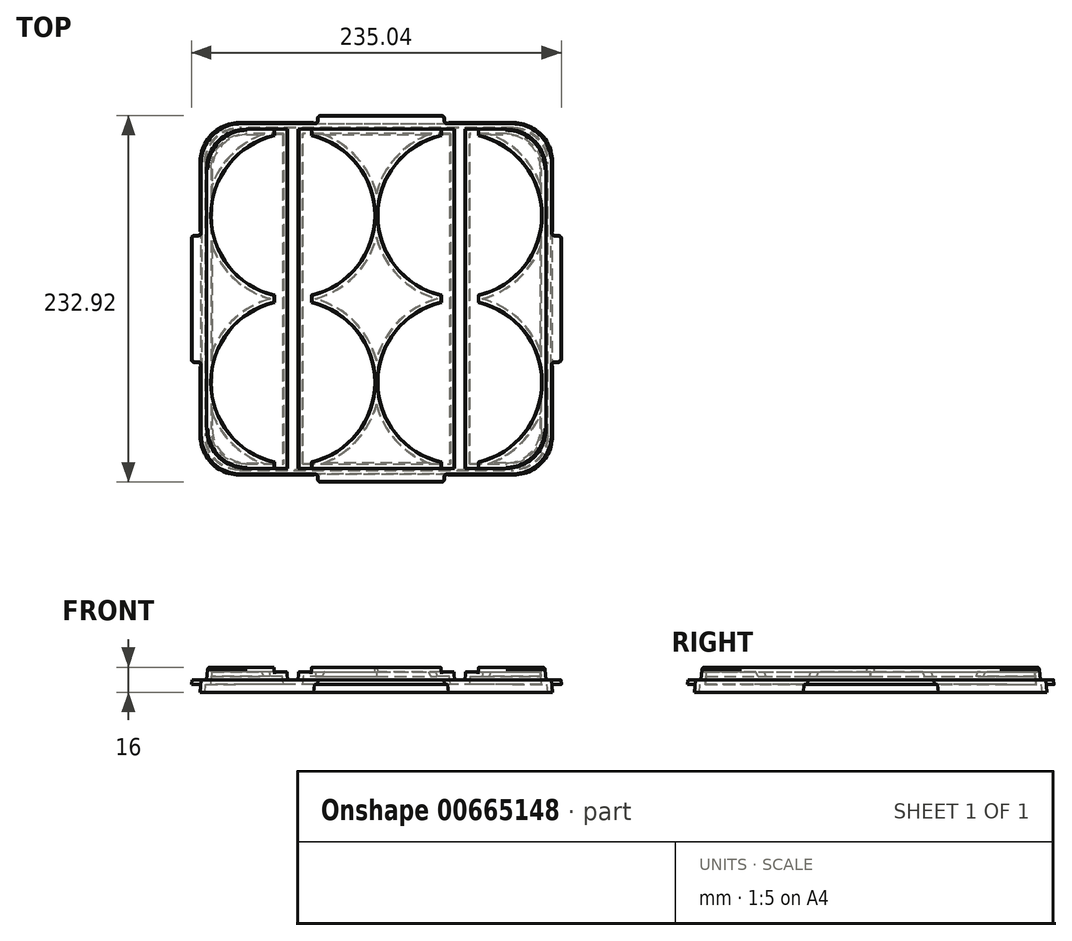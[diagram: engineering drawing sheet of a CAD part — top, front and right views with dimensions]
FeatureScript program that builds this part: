
annotation { "Feature Type Name" : "Feature", "Feature Type Description" : "" }
export const myFeature = defineFeature(function(context is Context, id is Id, definition is map)
    precondition{}
    {
        {
            var Q0;
            Q0=qCreatedBy(makeId("Top.planeOp"),FACE);
            var sketch = newSketch(context, id + "F0", { "sketchPlane" : qUnion([Q0])});
            skLineSegment(sketch, "E0", {"start": v(-53, 63.68) * mm, "end": v(-53, -68.5) * mm, "construction": true});
            skLineSegment(sketch, "E1", {"start": v(-108.87, 53) * mm, "end": v(91.95, 53) * mm, "construction": true});
            skLineSegment(sketch, "E2.MirrorCS", {"start": v(53, 63.68) * mm, "end": v(53, -68.5) * mm, "construction": true});
            skLineSegment(sketch, "E3.MirrorCS", {"start": v(-108.87, -53) * mm, "end": v(91.95, -53) * mm, "construction": true});
            skLineSegment(sketch, "E4", {"start": v(-107, 152.73) * mm, "end": v(-107, -156.18) * mm, "construction": true});
            skLineSegment(sketch, "E5", {"start": v(-201.2, -107) * mm, "end": v(310.8, -107) * mm, "construction": true});
            skLineSegment(sketch, "E6.MirrorCS", {"start": v(107, 152.73) * mm, "end": v(107, -156.18) * mm, "construction": true});
            skLineSegment(sketch, "E7.MirrorCS", {"start": v(-201.2, 107) * mm, "end": v(310.8, 107) * mm, "construction": true});
            skLineSegment(sketch, "E8.bottom", {"start": v(-107, 107) * mm, "end": v(107, 107) * mm});
            skLineSegment(sketch, "E8.top", {"start": v(-107, -107) * mm, "end": v(107, -107) * mm});
            skLineSegment(sketch, "E8.left", {"start": v(-107, 107) * mm, "end": v(-107, -107) * mm});
            skLineSegment(sketch, "E8.right", {"start": v(107, 107) * mm, "end": v(107, -107) * mm});
            skSolve(sketch);
        }
        {
            var Q0;
            Q0=makeQuery(id+"F0.imprint","IMPRINT",FACE,{"disambiguationData":[TD([[makeQuery(id+"F0.imprint","IMPRINT",EDGE,{"derivedFrom":sQuery(id+"F0.wireOp",EDGE,"E8.bottom")}),-1.0]])]});
            extrude(context, id + "F1", {"entities" : qUnion([Q0]), "oppositeDirection" : true, "depth" : 8 * mm, "offsetDistance" : 25 * mm, "hasDraft" : true, "draftAngle" : 5 * degree});
        }
        {
            var Q0;
            Q0=makeQuery(id+"F1.opExtrude","CAP_FACE",FACE,{"disambiguationData":[OSD([sQuery(id+"F0.wireOp",EDGE,"E8.bottom"),sQuery(id+"F0.wireOp",EDGE,"E8.top"),sQuery(id+"F0.wireOp",EDGE,"E8.left"),sQuery(id+"F0.wireOp",EDGE,"E8.right")])],"isStart":false});
            var sketch = newSketch(context, id + "F2", { "sketchPlane" : qUnion([Q0])});
            skLineSegment(sketch, "E9", {"start": v(-264, 111.2) * mm, "end": v(236, 111.2) * mm, "construction": true});
            skLineSegment(sketch, "E10.MirrorCS", {"start": v(-264, -111.2) * mm, "end": v(236, -111.2) * mm, "construction": true});
            skLineSegment(sketch, "E11", {"start": v(-111.2, 316.9) * mm, "end": v(-111.2, -183.1) * mm, "construction": true});
            skLineSegment(sketch, "E12.MirrorCS", {"start": v(111.2, 316.9) * mm, "end": v(111.2, -183.1) * mm, "construction": true});
            skLineSegment(sketch, "E13.bottom", {"start": v(-111.2, 111.2) * mm, "end": v(111.2, 111.2) * mm});
            skLineSegment(sketch, "E13.top", {"start": v(-111.2, -111.2) * mm, "end": v(111.2, -111.2) * mm});
            skLineSegment(sketch, "E13.left", {"start": v(-111.2, 111.2) * mm, "end": v(-111.2, -111.2) * mm});
            skLineSegment(sketch, "E13.right", {"start": v(111.2, 111.2) * mm, "end": v(111.2, -111.2) * mm});
            skSolve(sketch);
        }
        {
            var Q0;
            Q0=makeQuery(id+"F2.imprint","IMPRINT",FACE,{"disambiguationData":[TD([[makeQuery(id+"F2.imprint","IMPRINT",EDGE,{"derivedFrom":sQuery(id+"F2.wireOp",EDGE,"E13.bottom")}),-1.0]])]});
            var Q1;
            Q1=makeQuery(id+"F2.imprint","IMPRINT",FACE,{"disambiguationData":[TD([[makeQuery(id+"F2.imprint","IMPRINT",EDGE,{"derivedFrom":makeQuery(id+"F1.opExtrude","CAP_EDGE",EDGE,{"disambiguationData":[OSD([sQuery(id+"F0.wireOp",EDGE,"E8.bottom")])],"isStart":false})}),1.0]])]});
            extrude(context, id + "F3", {"entities" : qUnion([Q0, Q1]), "operationType" : NewBodyOperationType.ADD, "depth" : 8 * mm, "offsetDistance" : 25 * mm, "hasDraft" : true, "draftAngle" : 5 * degree});
        }
        {
            var Q0;
            Q0=makeQuery(id+"F1.opExtrude","CAP_FACE",FACE,{"disambiguationData":[OSD([sQuery(id+"F0.wireOp",EDGE,"E8.bottom"),sQuery(id+"F0.wireOp",EDGE,"E8.top"),sQuery(id+"F0.wireOp",EDGE,"E8.left"),sQuery(id+"F0.wireOp",EDGE,"E8.right")])],"isStart":true});
            var sketch = newSketch(context, id + "F4", { "sketchPlane" : qUnion([Q0])});
            skLineSegment(sketch, "E14", {"start": v(-107, 0) * mm, "end": v(107, 0) * mm, "construction": true});
            skLineSegment(sketch, "E15", {"start": v(-107, -53) * mm, "end": v(107, -53) * mm, "construction": true});
            skLineSegment(sketch, "E16.MirrorCS", {"start": v(-107, 53) * mm, "end": v(107, 53) * mm, "construction": true});
            skLineSegment(sketch, "E17", {"start": v(-53, -107) * mm, "end": v(-53, 107) * mm, "construction": true});
            skLineSegment(sketch, "E18", {"start": v(0, -107) * mm, "end": v(0, 107) * mm, "construction": true});
            skLineSegment(sketch, "E19.MirrorCS", {"start": v(53, -107) * mm, "end": v(53, 107) * mm, "construction": true});
            skCircle(sketch, "E20", {"center": v(-53, -53) * mm, "radius": 52.25 * mm});
            skCircle(sketch, "E21", {"center": v(-53, 53) * mm, "radius": 52.25 * mm});
            skCircle(sketch, "E22", {"center": v(53, 53) * mm, "radius": 52.25 * mm});
            skCircle(sketch, "E23", {"center": v(53, -53) * mm, "radius": 52.25 * mm});
            skLineSegment(sketch, "E24", {"start": v(65, 127) * mm, "end": v(65, 105.96) * mm});
            skLineSegment(sketch, "E25.MirrorCS", {"start": v(41, 107) * mm, "end": v(41, 105.96) * mm});
            skLineSegment(sketch, "E26.MirrorCS", {"start": v(-41, 107) * mm, "end": v(-41, 105.96) * mm});
            skLineSegment(sketch, "E27.MirrorCS", {"start": v(-65, 107) * mm, "end": v(-65, 105.96) * mm});
            skLineSegment(sketch, "E28.MirrorCS", {"start": v(41, -107) * mm, "end": v(41, -105.96) * mm});
            skLineSegment(sketch, "E29.MirrorCS", {"start": v(65, -107) * mm, "end": v(65, -105.96) * mm});
            skLineSegment(sketch, "E30.MirrorCS", {"start": v(-65, -107) * mm, "end": v(-65, -105.96) * mm});
            skLineSegment(sketch, "E31.MirrorCS", {"start": v(-41, -107) * mm, "end": v(-41, -105.96) * mm});
            skPoint(sketch, "E32.orphan", {"position": v(65, 107) * mm});
            skLineSegment(sketch, "E33.MirrorCS", {"start": v(41, 127) * mm, "end": v(41, 105.96) * mm});
            skLineSegment(sketch, "E34.MirrorCS", {"start": v(-41, 127) * mm, "end": v(-41, 105.96) * mm});
            skLineSegment(sketch, "E35.MirrorCS", {"start": v(-65, 127) * mm, "end": v(-65, 105.96) * mm});
            skLineSegment(sketch, "E36.MirrorCS", {"start": v(-41, -127) * mm, "end": v(-41, -105.96) * mm});
            skLineSegment(sketch, "E37.MirrorCS", {"start": v(-65, -127) * mm, "end": v(-65, -105.96) * mm});
            skLineSegment(sketch, "E38.MirrorCS", {"start": v(41, -127) * mm, "end": v(41, -105.96) * mm});
            skLineSegment(sketch, "E39.MirrorCS", {"start": v(65, -127) * mm, "end": v(65, -105.96) * mm});
            skLineSegment(sketch, "E40", {"start": v(-65, 127) * mm, "end": v(-41, 127) * mm});
            skLineSegment(sketch, "E41", {"start": v(41, 127) * mm, "end": v(65, 127) * mm});
            skLineSegment(sketch, "E42", {"start": v(-65, -127) * mm, "end": v(-41, -127) * mm});
            skLineSegment(sketch, "E43", {"start": v(41, -127) * mm, "end": v(65, -127) * mm});
            skLineSegment(sketch, "E44", {"start": v(-65, 105.96) * mm, "end": v(-65, -105.96) * mm});
            skLineSegment(sketch, "E45.MirrorCS", {"start": v(-41, 105.96) * mm, "end": v(-41, -105.96) * mm});
            skLineSegment(sketch, "E46.MirrorCS", {"start": v(41, 105.96) * mm, "end": v(41, -105.96) * mm});
            skLineSegment(sketch, "E47.MirrorCS", {"start": v(65, 105.96) * mm, "end": v(65, -105.96) * mm});
            skLineSegment(sketch, "E48", {"start": v(-57, 127) * mm, "end": v(-57, -127) * mm});
            skPoint(sketch, "E48.endSnap0", {"position": v(-53, -127) * mm});
            skLineSegment(sketch, "E49.MirrorCS", {"start": v(-49, 127) * mm, "end": v(-49, -127) * mm});
            skLineSegment(sketch, "E50.MirrorCS", {"start": v(49, 127) * mm, "end": v(49, -127) * mm});
            skLineSegment(sketch, "E51.MirrorCS", {"start": v(57, 127) * mm, "end": v(57, -127) * mm});
            skSolve(sketch);
        }
        {
            var Q0;
            {var subQ0=sQuery(id+"F4.wireOp",EDGE,"E34.MirrorCS");var subQ1=sQuery(id+"F4.wireOp",EDGE,"E21");var subQ2=makeQuery(id+"F4.imprint","INTERSECT",VERTEX,{"derivedFrom":[subQ1,subQ0]});Q0=makeQuery(id+"F4.imprint","IMPRINT",FACE,{"disambiguationData":[TD([[makeQuery(id+"F4.imprint","IMPRINT",EDGE,{"disambiguationData":[TD([[subQ2,1.0]])],"derivedFrom":subQ1}),1.0]])]});}
            var Q1;
            {var subQ0=sQuery(id+"F4.wireOp",EDGE,"E35.MirrorCS");var subQ1=sQuery(id+"F4.wireOp",EDGE,"E21");var subQ2=makeQuery(id+"F4.imprint","INTERSECT",VERTEX,{"derivedFrom":[subQ1,subQ0]});Q1=makeQuery(id+"F4.imprint","IMPRINT",FACE,{"disambiguationData":[TD([[makeQuery(id+"F4.imprint","IMPRINT",EDGE,{"disambiguationData":[TD([[subQ2,-1.0]])],"derivedFrom":subQ1}),1.0]])]});}
            var Q2;
            {var subQ3=sQuery(id+"F4.wireOp",EDGE,"E21");var subQ6=sQuery(id+"F4.wireOp",EDGE,"E48");var subQ7=makeQuery(id+"F4.imprint","INTERSECT",VERTEX,{"disambiguationData":[OD(0.0)],"derivedFrom":[subQ3,subQ6]});Q2=makeQuery(id+"F4.imprint","IMPRINT",FACE,{"disambiguationData":[TD([[makeQuery(id+"F4.imprint","IMPRINT",EDGE,{"disambiguationData":[TD([[subQ7,-1.0]])],"derivedFrom":subQ3}),1.0]])]});}
            var Q3;
            {var subQ3=sQuery(id+"F4.wireOp",EDGE,"E21");var subQ6=sQuery(id+"F4.wireOp",EDGE,"E49.MirrorCS");var subQ8=makeQuery(id+"F4.imprint","INTERSECT",VERTEX,{"disambiguationData":[OD(0.0)],"derivedFrom":[subQ3,subQ6]});Q3=makeQuery(id+"F4.imprint","IMPRINT",FACE,{"disambiguationData":[TD([[makeQuery(id+"F4.imprint","IMPRINT",EDGE,{"disambiguationData":[TD([[subQ8,1.0]])],"derivedFrom":subQ3}),1.0]])]});}
            var Q4;
            {var subQ0=sQuery(id+"F4.wireOp",EDGE,"E49.MirrorCS");var subQ1=sQuery(id+"F4.wireOp",EDGE,"E21");var subQ2=makeQuery(id+"F4.imprint","INTERSECT",VERTEX,{"disambiguationData":[OD(0.0)],"derivedFrom":[subQ1,subQ0]});Q4=makeQuery(id+"F4.imprint","IMPRINT",FACE,{"disambiguationData":[TD([[makeQuery(id+"F4.imprint","IMPRINT",EDGE,{"disambiguationData":[TD([[subQ2,-1.0]])],"derivedFrom":subQ1}),1.0]])]});}
            var Q5;
            {var subQ0=sQuery(id+"F4.wireOp",EDGE,"E33.MirrorCS");var subQ1=sQuery(id+"F4.wireOp",EDGE,"E22");var subQ2=makeQuery(id+"F4.imprint","INTERSECT",VERTEX,{"derivedFrom":[subQ1,subQ0]});Q5=makeQuery(id+"F4.imprint","IMPRINT",FACE,{"disambiguationData":[TD([[makeQuery(id+"F4.imprint","IMPRINT",EDGE,{"disambiguationData":[TD([[subQ2,-1.0]])],"derivedFrom":subQ1}),1.0]])]});}
            var Q6;
            {var subQ3=sQuery(id+"F4.wireOp",EDGE,"E22");var subQ5=sQuery(id+"F4.wireOp",EDGE,"E50.MirrorCS");var subQ6=makeQuery(id+"F4.imprint","INTERSECT",VERTEX,{"disambiguationData":[OD(0.0)],"derivedFrom":[subQ3,subQ5]});Q6=makeQuery(id+"F4.imprint","IMPRINT",FACE,{"disambiguationData":[TD([[makeQuery(id+"F4.imprint","IMPRINT",EDGE,{"disambiguationData":[TD([[subQ6,-1.0]])],"derivedFrom":subQ3}),1.0]])]});}
            var Q7;
            {var subQ3=sQuery(id+"F4.wireOp",EDGE,"E22");var subQ6=sQuery(id+"F4.wireOp",EDGE,"E51.MirrorCS");var subQ8=makeQuery(id+"F4.imprint","INTERSECT",VERTEX,{"disambiguationData":[OD(0.0)],"derivedFrom":[subQ3,subQ6]});Q7=makeQuery(id+"F4.imprint","IMPRINT",FACE,{"disambiguationData":[TD([[makeQuery(id+"F4.imprint","IMPRINT",EDGE,{"disambiguationData":[TD([[subQ8,1.0]])],"derivedFrom":subQ3}),1.0]])]});}
            var Q8;
            {var subQ0=sQuery(id+"F4.wireOp",EDGE,"E51.MirrorCS");var subQ1=sQuery(id+"F4.wireOp",EDGE,"E22");var subQ2=makeQuery(id+"F4.imprint","INTERSECT",VERTEX,{"disambiguationData":[OD(0.0)],"derivedFrom":[subQ1,subQ0]});Q8=makeQuery(id+"F4.imprint","IMPRINT",FACE,{"disambiguationData":[TD([[makeQuery(id+"F4.imprint","IMPRINT",EDGE,{"disambiguationData":[TD([[subQ2,-1.0]])],"derivedFrom":subQ1}),1.0]])]});}
            var Q9;
            {var subQ0=sQuery(id+"F4.wireOp",EDGE,"E24");var subQ1=sQuery(id+"F4.wireOp",EDGE,"E22");var subQ2=makeQuery(id+"F4.imprint","INTERSECT",VERTEX,{"derivedFrom":[subQ1,subQ0]});Q9=makeQuery(id+"F4.imprint","IMPRINT",FACE,{"disambiguationData":[TD([[makeQuery(id+"F4.imprint","IMPRINT",EDGE,{"disambiguationData":[TD([[subQ2,1.0]])],"derivedFrom":subQ1}),1.0]])]});}
            var Q10;
            {var subQ0=sQuery(id+"F4.wireOp",EDGE,"E44");var subQ1=sQuery(id+"F4.wireOp",EDGE,"E20");var subQ2=makeQuery(id+"F4.imprint","INTERSECT",VERTEX,{"derivedFrom":[subQ1,subQ0]});Q10=makeQuery(id+"F4.imprint","IMPRINT",FACE,{"disambiguationData":[TD([[makeQuery(id+"F4.imprint","IMPRINT",EDGE,{"disambiguationData":[TD([[subQ2,-1.0]])],"derivedFrom":subQ1}),1.0]])]});}
            var Q11;
            {var subQ3=sQuery(id+"F4.wireOp",EDGE,"E20");var subQ6=sQuery(id+"F4.wireOp",EDGE,"E48");var subQ8=makeQuery(id+"F4.imprint","INTERSECT",VERTEX,{"disambiguationData":[OD(0.0)],"derivedFrom":[subQ3,subQ6]});Q11=makeQuery(id+"F4.imprint","IMPRINT",FACE,{"disambiguationData":[TD([[makeQuery(id+"F4.imprint","IMPRINT",EDGE,{"disambiguationData":[TD([[subQ8,-1.0]])],"derivedFrom":subQ3}),1.0]])]});}
            var Q12;
            {var subQ0=sQuery(id+"F4.wireOp",EDGE,"E49.MirrorCS");var subQ1=sQuery(id+"F4.wireOp",EDGE,"E20");var subQ2=makeQuery(id+"F4.imprint","INTERSECT",VERTEX,{"disambiguationData":[OD(0.0)],"derivedFrom":[subQ1,subQ0]});Q12=makeQuery(id+"F4.imprint","IMPRINT",FACE,{"disambiguationData":[TD([[makeQuery(id+"F4.imprint","IMPRINT",EDGE,{"disambiguationData":[TD([[subQ2,-1.0]])],"derivedFrom":subQ1}),1.0]])]});}
            var Q13;
            {var subQ3=sQuery(id+"F4.wireOp",EDGE,"E20");var subQ6=sQuery(id+"F4.wireOp",EDGE,"E49.MirrorCS");var subQ8=makeQuery(id+"F4.imprint","INTERSECT",VERTEX,{"disambiguationData":[OD(0.0)],"derivedFrom":[subQ3,subQ6]});Q13=makeQuery(id+"F4.imprint","IMPRINT",FACE,{"disambiguationData":[TD([[makeQuery(id+"F4.imprint","IMPRINT",EDGE,{"disambiguationData":[TD([[subQ8,1.0]])],"derivedFrom":subQ3}),1.0]])]});}
            var Q14;
            {var subQ0=sQuery(id+"F4.wireOp",EDGE,"E45.MirrorCS");var subQ1=sQuery(id+"F4.wireOp",EDGE,"E20");var subQ2=makeQuery(id+"F4.imprint","INTERSECT",VERTEX,{"derivedFrom":[subQ1,subQ0]});Q14=makeQuery(id+"F4.imprint","IMPRINT",FACE,{"disambiguationData":[TD([[makeQuery(id+"F4.imprint","IMPRINT",EDGE,{"disambiguationData":[TD([[subQ2,1.0]])],"derivedFrom":subQ1}),1.0]])]});}
            var Q15;
            {var subQ0=sQuery(id+"F4.wireOp",EDGE,"E46.MirrorCS");var subQ1=sQuery(id+"F4.wireOp",EDGE,"E23");var subQ2=makeQuery(id+"F4.imprint","INTERSECT",VERTEX,{"derivedFrom":[subQ1,subQ0]});Q15=makeQuery(id+"F4.imprint","IMPRINT",FACE,{"disambiguationData":[TD([[makeQuery(id+"F4.imprint","IMPRINT",EDGE,{"disambiguationData":[TD([[subQ2,-1.0]])],"derivedFrom":subQ1}),1.0]])]});}
            var Q16;
            {var subQ3=sQuery(id+"F4.wireOp",EDGE,"E23");var subQ5=sQuery(id+"F4.wireOp",EDGE,"E50.MirrorCS");var subQ8=makeQuery(id+"F4.imprint","INTERSECT",VERTEX,{"disambiguationData":[OD(0.0)],"derivedFrom":[subQ3,subQ5]});Q16=makeQuery(id+"F4.imprint","IMPRINT",FACE,{"disambiguationData":[TD([[makeQuery(id+"F4.imprint","IMPRINT",EDGE,{"disambiguationData":[TD([[subQ8,-1.0]])],"derivedFrom":subQ3}),1.0]])]});}
            var Q17;
            {var subQ0=sQuery(id+"F4.wireOp",EDGE,"E51.MirrorCS");var subQ1=sQuery(id+"F4.wireOp",EDGE,"E23");var subQ2=makeQuery(id+"F4.imprint","INTERSECT",VERTEX,{"disambiguationData":[OD(0.0)],"derivedFrom":[subQ1,subQ0]});Q17=makeQuery(id+"F4.imprint","IMPRINT",FACE,{"disambiguationData":[TD([[makeQuery(id+"F4.imprint","IMPRINT",EDGE,{"disambiguationData":[TD([[subQ2,-1.0]])],"derivedFrom":subQ1}),1.0]])]});}
            var Q18;
            {var subQ3=sQuery(id+"F4.wireOp",EDGE,"E23");var subQ5=sQuery(id+"F4.wireOp",EDGE,"E51.MirrorCS");var subQ8=makeQuery(id+"F4.imprint","INTERSECT",VERTEX,{"disambiguationData":[OD(0.0)],"derivedFrom":[subQ3,subQ5]});Q18=makeQuery(id+"F4.imprint","IMPRINT",FACE,{"disambiguationData":[TD([[makeQuery(id+"F4.imprint","IMPRINT",EDGE,{"disambiguationData":[TD([[subQ8,1.0]])],"derivedFrom":subQ3}),1.0]])]});}
            var Q19;
            {var subQ0=sQuery(id+"F4.wireOp",EDGE,"E47.MirrorCS");var subQ1=sQuery(id+"F4.wireOp",EDGE,"E23");var subQ2=makeQuery(id+"F4.imprint","INTERSECT",VERTEX,{"derivedFrom":[subQ1,subQ0]});Q19=makeQuery(id+"F4.imprint","IMPRINT",FACE,{"disambiguationData":[TD([[makeQuery(id+"F4.imprint","IMPRINT",EDGE,{"disambiguationData":[TD([[subQ2,1.0]])],"derivedFrom":subQ1}),1.0]])]});}
            var Q20;
            {var subQ0=sQuery(id+"F4.wireOp",EDGE,"E48");var subQ1=sQuery(id+"F4.wireOp",EDGE,"E21");var subQ2=makeQuery(id+"F4.imprint","INTERSECT",VERTEX,{"disambiguationData":[OD(0.0)],"derivedFrom":[subQ1,subQ0]});Q20=makeQuery(id+"F4.imprint","IMPRINT",FACE,{"disambiguationData":[TD([[makeQuery(id+"F4.imprint","IMPRINT",EDGE,{"disambiguationData":[TD([[subQ2,-1.0]])],"derivedFrom":subQ1}),-1.0]])]});}
            var Q21;
            {var subQ0=sQuery(id+"F4.wireOp",EDGE,"E49.MirrorCS");var subQ1=sQuery(id+"F4.wireOp",EDGE,"E21");var subQ2=makeQuery(id+"F4.imprint","INTERSECT",VERTEX,{"disambiguationData":[OD(0.0)],"derivedFrom":[subQ1,subQ0]});Q21=makeQuery(id+"F4.imprint","IMPRINT",FACE,{"disambiguationData":[TD([[makeQuery(id+"F4.imprint","IMPRINT",EDGE,{"disambiguationData":[TD([[subQ2,-1.0]])],"derivedFrom":subQ1}),-1.0]])]});}
            var Q22;
            {var subQ0=sQuery(id+"F4.wireOp",EDGE,"E49.MirrorCS");var subQ1=sQuery(id+"F4.wireOp",EDGE,"E21");var subQ2=makeQuery(id+"F4.imprint","INTERSECT",VERTEX,{"disambiguationData":[OD(0.0)],"derivedFrom":[subQ1,subQ0]});Q22=makeQuery(id+"F4.imprint","IMPRINT",FACE,{"disambiguationData":[TD([[makeQuery(id+"F4.imprint","IMPRINT",EDGE,{"disambiguationData":[TD([[subQ2,1.0]])],"derivedFrom":subQ1}),-1.0]])]});}
            var Q23;
            {var subQ0=sQuery(id+"F4.wireOp",EDGE,"E40");var subQ1=sQuery(id+"F4.wireOp",EDGE,"E35.MirrorCS");var subQ2=makeQuery(id+"F4.imprint","INTERSECT",VERTEX,{"derivedFrom":[subQ1,subQ0]});Q23=makeQuery(id+"F4.imprint","IMPRINT",FACE,{"disambiguationData":[TD([[makeQuery(id+"F4.imprint","IMPRINT",EDGE,{"disambiguationData":[TD([[subQ2,-1.0]])],"derivedFrom":subQ1}),1.0]])]});}
            var Q24;
            {var subQ0=sQuery(id+"F4.wireOp",EDGE,"E48");var subQ1=sQuery(id+"F4.wireOp",EDGE,"E40");var subQ2=makeQuery(id+"F4.imprint","INTERSECT",VERTEX,{"derivedFrom":[subQ1,subQ0]});Q24=makeQuery(id+"F4.imprint","IMPRINT",FACE,{"disambiguationData":[TD([[makeQuery(id+"F4.imprint","IMPRINT",EDGE,{"disambiguationData":[TD([[subQ2,-1.0]])],"derivedFrom":subQ1}),-1.0]])]});}
            var Q25;
            {var subQ0=sQuery(id+"F4.wireOp",EDGE,"E40");var subQ1=sQuery(id+"F4.wireOp",EDGE,"E34.MirrorCS");var subQ2=makeQuery(id+"F4.imprint","INTERSECT",VERTEX,{"derivedFrom":[subQ1,subQ0]});Q25=makeQuery(id+"F4.imprint","IMPRINT",FACE,{"disambiguationData":[TD([[makeQuery(id+"F4.imprint","IMPRINT",EDGE,{"disambiguationData":[TD([[subQ2,-1.0]])],"derivedFrom":subQ1}),-1.0]])]});}
            var Q26;
            {var subQ0=sQuery(id+"F4.wireOp",EDGE,"E48");var subQ1=sQuery(id+"F4.wireOp",EDGE,"E20");var subQ2=makeQuery(id+"F4.imprint","INTERSECT",VERTEX,{"disambiguationData":[OD(0.0)],"derivedFrom":[subQ1,subQ0]});Q26=makeQuery(id+"F4.imprint","IMPRINT",FACE,{"disambiguationData":[TD([[makeQuery(id+"F4.imprint","IMPRINT",EDGE,{"disambiguationData":[TD([[subQ2,-1.0]])],"derivedFrom":subQ1}),-1.0]])]});}
            var Q27;
            {var subQ0=sQuery(id+"F4.wireOp",EDGE,"E49.MirrorCS");var subQ1=sQuery(id+"F4.wireOp",EDGE,"E20");var subQ2=makeQuery(id+"F4.imprint","INTERSECT",VERTEX,{"disambiguationData":[OD(0.0)],"derivedFrom":[subQ1,subQ0]});Q27=makeQuery(id+"F4.imprint","IMPRINT",FACE,{"disambiguationData":[TD([[makeQuery(id+"F4.imprint","IMPRINT",EDGE,{"disambiguationData":[TD([[subQ2,-1.0]])],"derivedFrom":subQ1}),-1.0]])]});}
            var Q28;
            {var subQ0=sQuery(id+"F4.wireOp",EDGE,"E49.MirrorCS");var subQ1=sQuery(id+"F4.wireOp",EDGE,"E20");var subQ2=makeQuery(id+"F4.imprint","INTERSECT",VERTEX,{"disambiguationData":[OD(0.0)],"derivedFrom":[subQ1,subQ0]});Q28=makeQuery(id+"F4.imprint","IMPRINT",FACE,{"disambiguationData":[TD([[makeQuery(id+"F4.imprint","IMPRINT",EDGE,{"disambiguationData":[TD([[subQ2,1.0]])],"derivedFrom":subQ1}),-1.0]])]});}
            var Q29;
            {var subQ0=sQuery(id+"F4.wireOp",EDGE,"E41");var subQ1=sQuery(id+"F4.wireOp",EDGE,"E33.MirrorCS");var subQ2=makeQuery(id+"F4.imprint","INTERSECT",VERTEX,{"derivedFrom":[subQ1,subQ0]});Q29=makeQuery(id+"F4.imprint","IMPRINT",FACE,{"disambiguationData":[TD([[makeQuery(id+"F4.imprint","IMPRINT",EDGE,{"disambiguationData":[TD([[subQ2,-1.0]])],"derivedFrom":subQ1}),1.0]])]});}
            var Q30;
            {var subQ0=sQuery(id+"F4.wireOp",EDGE,"E50.MirrorCS");var subQ1=sQuery(id+"F4.wireOp",EDGE,"E41");var subQ2=makeQuery(id+"F4.imprint","INTERSECT",VERTEX,{"derivedFrom":[subQ1,subQ0]});Q30=makeQuery(id+"F4.imprint","IMPRINT",FACE,{"disambiguationData":[TD([[makeQuery(id+"F4.imprint","IMPRINT",EDGE,{"disambiguationData":[TD([[subQ2,-1.0]])],"derivedFrom":subQ1}),-1.0]])]});}
            var Q31;
            {var subQ0=sQuery(id+"F4.wireOp",EDGE,"E41");var subQ1=sQuery(id+"F4.wireOp",EDGE,"E24");var subQ2=makeQuery(id+"F4.imprint","INTERSECT",VERTEX,{"derivedFrom":[subQ1,subQ0]});Q31=makeQuery(id+"F4.imprint","IMPRINT",FACE,{"disambiguationData":[TD([[makeQuery(id+"F4.imprint","IMPRINT",EDGE,{"disambiguationData":[TD([[subQ2,-1.0]])],"derivedFrom":subQ1}),-1.0]])]});}
            var Q32;
            {var subQ0=sQuery(id+"F4.wireOp",EDGE,"E50.MirrorCS");var subQ1=sQuery(id+"F4.wireOp",EDGE,"E22");var subQ2=makeQuery(id+"F4.imprint","INTERSECT",VERTEX,{"disambiguationData":[OD(0.0)],"derivedFrom":[subQ1,subQ0]});Q32=makeQuery(id+"F4.imprint","IMPRINT",FACE,{"disambiguationData":[TD([[makeQuery(id+"F4.imprint","IMPRINT",EDGE,{"disambiguationData":[TD([[subQ2,-1.0]])],"derivedFrom":subQ1}),-1.0]])]});}
            var Q33;
            {var subQ0=sQuery(id+"F4.wireOp",EDGE,"E51.MirrorCS");var subQ1=sQuery(id+"F4.wireOp",EDGE,"E22");var subQ2=makeQuery(id+"F4.imprint","INTERSECT",VERTEX,{"disambiguationData":[OD(0.0)],"derivedFrom":[subQ1,subQ0]});Q33=makeQuery(id+"F4.imprint","IMPRINT",FACE,{"disambiguationData":[TD([[makeQuery(id+"F4.imprint","IMPRINT",EDGE,{"disambiguationData":[TD([[subQ2,-1.0]])],"derivedFrom":subQ1}),-1.0]])]});}
            var Q34;
            {var subQ0=sQuery(id+"F4.wireOp",EDGE,"E51.MirrorCS");var subQ1=sQuery(id+"F4.wireOp",EDGE,"E22");var subQ2=makeQuery(id+"F4.imprint","INTERSECT",VERTEX,{"disambiguationData":[OD(0.0)],"derivedFrom":[subQ1,subQ0]});Q34=makeQuery(id+"F4.imprint","IMPRINT",FACE,{"disambiguationData":[TD([[makeQuery(id+"F4.imprint","IMPRINT",EDGE,{"disambiguationData":[TD([[subQ2,1.0]])],"derivedFrom":subQ1}),-1.0]])]});}
            var Q35;
            {var subQ0=sQuery(id+"F4.wireOp",EDGE,"E46.MirrorCS");var subQ1=sQuery(id+"F4.wireOp",EDGE,"E22");var subQ2=makeQuery(id+"F4.imprint","INTERSECT",VERTEX,{"derivedFrom":[subQ1,subQ0]});Q35=makeQuery(id+"F4.imprint","IMPRINT",FACE,{"disambiguationData":[TD([[makeQuery(id+"F4.imprint","IMPRINT",EDGE,{"disambiguationData":[TD([[subQ2,-1.0]])],"derivedFrom":subQ1}),-1.0]])]});}
            var Q36;
            {var subQ0=sQuery(id+"F4.wireOp",EDGE,"E50.MirrorCS");var subQ1=sQuery(id+"F4.wireOp",EDGE,"E22");var subQ2=makeQuery(id+"F4.imprint","INTERSECT",VERTEX,{"disambiguationData":[OD(1.0)],"derivedFrom":[subQ1,subQ0]});Q36=makeQuery(id+"F4.imprint","IMPRINT",FACE,{"disambiguationData":[TD([[makeQuery(id+"F4.imprint","IMPRINT",EDGE,{"disambiguationData":[TD([[subQ2,-1.0]])],"derivedFrom":subQ1}),-1.0]])]});}
            var Q37;
            {var subQ0=sQuery(id+"F4.wireOp",EDGE,"E51.MirrorCS");var subQ1=sQuery(id+"F4.wireOp",EDGE,"E22");var subQ2=makeQuery(id+"F4.imprint","INTERSECT",VERTEX,{"disambiguationData":[OD(1.0)],"derivedFrom":[subQ1,subQ0]});Q37=makeQuery(id+"F4.imprint","IMPRINT",FACE,{"disambiguationData":[TD([[makeQuery(id+"F4.imprint","IMPRINT",EDGE,{"disambiguationData":[TD([[subQ2,-1.0]])],"derivedFrom":subQ1}),-1.0]])]});}
            var Q38;
            {var subQ0=sQuery(id+"F4.wireOp",EDGE,"E42");var subQ1=sQuery(id+"F4.wireOp",EDGE,"E37.MirrorCS");var subQ2=makeQuery(id+"F4.imprint","INTERSECT",VERTEX,{"derivedFrom":[subQ1,subQ0]});Q38=makeQuery(id+"F4.imprint","IMPRINT",FACE,{"disambiguationData":[TD([[makeQuery(id+"F4.imprint","IMPRINT",EDGE,{"disambiguationData":[TD([[subQ2,-1.0]])],"derivedFrom":subQ1}),-1.0]])]});}
            var Q39;
            {var subQ0=sQuery(id+"F4.wireOp",EDGE,"E48");var subQ1=sQuery(id+"F4.wireOp",EDGE,"E42");var subQ2=makeQuery(id+"F4.imprint","INTERSECT",VERTEX,{"derivedFrom":[subQ1,subQ0]});Q39=makeQuery(id+"F4.imprint","IMPRINT",FACE,{"disambiguationData":[TD([[makeQuery(id+"F4.imprint","IMPRINT",EDGE,{"disambiguationData":[TD([[subQ2,-1.0]])],"derivedFrom":subQ1}),1.0]])]});}
            var Q40;
            {var subQ0=sQuery(id+"F4.wireOp",EDGE,"E42");var subQ1=sQuery(id+"F4.wireOp",EDGE,"E36.MirrorCS");var subQ2=makeQuery(id+"F4.imprint","INTERSECT",VERTEX,{"derivedFrom":[subQ1,subQ0]});Q40=makeQuery(id+"F4.imprint","IMPRINT",FACE,{"disambiguationData":[TD([[makeQuery(id+"F4.imprint","IMPRINT",EDGE,{"disambiguationData":[TD([[subQ2,-1.0]])],"derivedFrom":subQ1}),1.0]])]});}
            var Q41;
            {var subQ0=sQuery(id+"F4.wireOp",EDGE,"E37.MirrorCS");var subQ1=sQuery(id+"F4.wireOp",EDGE,"E20");var subQ2=makeQuery(id+"F4.imprint","INTERSECT",VERTEX,{"derivedFrom":[subQ1,subQ0]});Q41=makeQuery(id+"F4.imprint","IMPRINT",FACE,{"disambiguationData":[TD([[makeQuery(id+"F4.imprint","IMPRINT",EDGE,{"disambiguationData":[TD([[subQ2,-1.0]])],"derivedFrom":subQ1}),-1.0]])]});}
            var Q42;
            {var subQ0=sQuery(id+"F4.wireOp",EDGE,"E48");var subQ1=sQuery(id+"F4.wireOp",EDGE,"E20");var subQ2=makeQuery(id+"F4.imprint","INTERSECT",VERTEX,{"disambiguationData":[OD(1.0)],"derivedFrom":[subQ1,subQ0]});Q42=makeQuery(id+"F4.imprint","IMPRINT",FACE,{"disambiguationData":[TD([[makeQuery(id+"F4.imprint","IMPRINT",EDGE,{"disambiguationData":[TD([[subQ2,-1.0]])],"derivedFrom":subQ1}),-1.0]])]});}
            var Q43;
            {var subQ0=sQuery(id+"F4.wireOp",EDGE,"E49.MirrorCS");var subQ1=sQuery(id+"F4.wireOp",EDGE,"E20");var subQ2=makeQuery(id+"F4.imprint","INTERSECT",VERTEX,{"disambiguationData":[OD(1.0)],"derivedFrom":[subQ1,subQ0]});Q43=makeQuery(id+"F4.imprint","IMPRINT",FACE,{"disambiguationData":[TD([[makeQuery(id+"F4.imprint","IMPRINT",EDGE,{"disambiguationData":[TD([[subQ2,-1.0]])],"derivedFrom":subQ1}),-1.0]])]});}
            var Q44;
            {var subQ0=sQuery(id+"F4.wireOp",EDGE,"E38.MirrorCS");var subQ1=sQuery(id+"F4.wireOp",EDGE,"E23");var subQ2=makeQuery(id+"F4.imprint","INTERSECT",VERTEX,{"derivedFrom":[subQ1,subQ0]});Q44=makeQuery(id+"F4.imprint","IMPRINT",FACE,{"disambiguationData":[TD([[makeQuery(id+"F4.imprint","IMPRINT",EDGE,{"disambiguationData":[TD([[subQ2,-1.0]])],"derivedFrom":subQ1}),-1.0]])]});}
            var Q45;
            {var subQ0=sQuery(id+"F4.wireOp",EDGE,"E50.MirrorCS");var subQ1=sQuery(id+"F4.wireOp",EDGE,"E23");var subQ2=makeQuery(id+"F4.imprint","INTERSECT",VERTEX,{"disambiguationData":[OD(1.0)],"derivedFrom":[subQ1,subQ0]});Q45=makeQuery(id+"F4.imprint","IMPRINT",FACE,{"disambiguationData":[TD([[makeQuery(id+"F4.imprint","IMPRINT",EDGE,{"disambiguationData":[TD([[subQ2,-1.0]])],"derivedFrom":subQ1}),-1.0]])]});}
            var Q46;
            {var subQ0=sQuery(id+"F4.wireOp",EDGE,"E51.MirrorCS");var subQ1=sQuery(id+"F4.wireOp",EDGE,"E23");var subQ2=makeQuery(id+"F4.imprint","INTERSECT",VERTEX,{"disambiguationData":[OD(1.0)],"derivedFrom":[subQ1,subQ0]});Q46=makeQuery(id+"F4.imprint","IMPRINT",FACE,{"disambiguationData":[TD([[makeQuery(id+"F4.imprint","IMPRINT",EDGE,{"disambiguationData":[TD([[subQ2,-1.0]])],"derivedFrom":subQ1}),-1.0]])]});}
            var Q47;
            {var subQ0=sQuery(id+"F4.wireOp",EDGE,"E43");var subQ1=sQuery(id+"F4.wireOp",EDGE,"E38.MirrorCS");var subQ2=makeQuery(id+"F4.imprint","INTERSECT",VERTEX,{"derivedFrom":[subQ1,subQ0]});Q47=makeQuery(id+"F4.imprint","IMPRINT",FACE,{"disambiguationData":[TD([[makeQuery(id+"F4.imprint","IMPRINT",EDGE,{"disambiguationData":[TD([[subQ2,-1.0]])],"derivedFrom":subQ1}),-1.0]])]});}
            var Q48;
            {var subQ0=sQuery(id+"F4.wireOp",EDGE,"E50.MirrorCS");var subQ1=sQuery(id+"F4.wireOp",EDGE,"E43");var subQ2=makeQuery(id+"F4.imprint","INTERSECT",VERTEX,{"derivedFrom":[subQ1,subQ0]});Q48=makeQuery(id+"F4.imprint","IMPRINT",FACE,{"disambiguationData":[TD([[makeQuery(id+"F4.imprint","IMPRINT",EDGE,{"disambiguationData":[TD([[subQ2,-1.0]])],"derivedFrom":subQ1}),1.0]])]});}
            var Q49;
            {var subQ0=sQuery(id+"F4.wireOp",EDGE,"E43");var subQ1=sQuery(id+"F4.wireOp",EDGE,"E39.MirrorCS");var subQ2=makeQuery(id+"F4.imprint","INTERSECT",VERTEX,{"derivedFrom":[subQ1,subQ0]});Q49=makeQuery(id+"F4.imprint","IMPRINT",FACE,{"disambiguationData":[TD([[makeQuery(id+"F4.imprint","IMPRINT",EDGE,{"disambiguationData":[TD([[subQ2,-1.0]])],"derivedFrom":subQ1}),1.0]])]});}
            var Q50;
            {var subQ0=sQuery(id+"F4.wireOp",EDGE,"E45.MirrorCS");var subQ1=sQuery(id+"F4.wireOp",EDGE,"E21");var subQ2=makeQuery(id+"F4.imprint","INTERSECT",VERTEX,{"disambiguationData":[OD(0.0)],"derivedFrom":[subQ1,subQ0]});Q50=makeQuery(id+"F4.imprint","IMPRINT",FACE,{"disambiguationData":[TD([[makeQuery(id+"F4.imprint","IMPRINT",EDGE,{"disambiguationData":[TD([[subQ2,1.0]])],"derivedFrom":subQ1}),1.0]])]});}
            var Q51;
            {var subQ0=sQuery(id+"F4.wireOp",EDGE,"E44");var subQ1=sQuery(id+"F4.wireOp",EDGE,"E21");var subQ2=makeQuery(id+"F4.imprint","INTERSECT",VERTEX,{"disambiguationData":[OD(0.0)],"derivedFrom":[subQ1,subQ0]});Q51=makeQuery(id+"F4.imprint","IMPRINT",FACE,{"disambiguationData":[TD([[makeQuery(id+"F4.imprint","IMPRINT",EDGE,{"disambiguationData":[TD([[subQ2,-1.0]])],"derivedFrom":subQ1}),1.0]])]});}
            var Q52;
            {var subQ0=sQuery(id+"F4.wireOp",EDGE,"E46.MirrorCS");var subQ1=sQuery(id+"F4.wireOp",EDGE,"E22");var subQ2=makeQuery(id+"F4.imprint","INTERSECT",VERTEX,{"disambiguationData":[OD(0.0)],"derivedFrom":[subQ1,subQ0]});Q52=makeQuery(id+"F4.imprint","IMPRINT",FACE,{"disambiguationData":[TD([[makeQuery(id+"F4.imprint","IMPRINT",EDGE,{"disambiguationData":[TD([[subQ2,-1.0]])],"derivedFrom":subQ1}),1.0]])]});}
            var Q53;
            {var subQ0=sQuery(id+"F4.wireOp",EDGE,"E47.MirrorCS");var subQ1=sQuery(id+"F4.wireOp",EDGE,"E22");var subQ2=makeQuery(id+"F4.imprint","INTERSECT",VERTEX,{"disambiguationData":[OD(0.0)],"derivedFrom":[subQ1,subQ0]});Q53=makeQuery(id+"F4.imprint","IMPRINT",FACE,{"disambiguationData":[TD([[makeQuery(id+"F4.imprint","IMPRINT",EDGE,{"disambiguationData":[TD([[subQ2,1.0]])],"derivedFrom":subQ1}),1.0]])]});}
            var Q54;
            {var subQ1=sQuery(id+"F4.wireOp",EDGE,"E23");var subQ5=sQuery(id+"F4.wireOp",EDGE,"E46.MirrorCS");var subQ8=makeQuery(id+"F4.imprint","INTERSECT",VERTEX,{"disambiguationData":[OD(1.0)],"derivedFrom":[subQ1,subQ5]});Q54=makeQuery(id+"F4.imprint","IMPRINT",FACE,{"disambiguationData":[TD([[makeQuery(id+"F4.imprint","IMPRINT",EDGE,{"disambiguationData":[TD([[subQ8,-1.0]])],"derivedFrom":subQ1}),-1.0]])]});}
            var Q55;
            {var subQ1=sQuery(id+"F4.wireOp",EDGE,"E20");var subQ5=sQuery(id+"F4.wireOp",EDGE,"E44");var subQ9=makeQuery(id+"F4.imprint","INTERSECT",VERTEX,{"disambiguationData":[OD(1.0)],"derivedFrom":[subQ1,subQ5]});Q55=makeQuery(id+"F4.imprint","IMPRINT",FACE,{"disambiguationData":[TD([[makeQuery(id+"F4.imprint","IMPRINT",EDGE,{"disambiguationData":[TD([[subQ9,-1.0]])],"derivedFrom":subQ1}),-1.0]])]});}
            extrude(context, id + "F5", {"entities" : qUnion([Q0, Q1, Q2, Q3, Q4, Q5, Q6, Q7, Q8, Q9, Q10, Q11, Q12, Q13, Q14, Q15, Q16, Q17, Q18, Q19, Q20, Q21, Q22, Q23, Q24, Q25, Q26, Q27, Q28, Q29, Q30, Q31, Q32, Q33, Q34, Q35, Q36, Q37, Q38, Q39, Q40, Q41, Q42, Q43, Q44, Q45, Q46, Q47, Q48, Q49, Q50, Q51, Q52, Q53, Q54, Q55]), "operationType" : NewBodyOperationType.REMOVE, "oppositeDirection" : true, "depth" : 3 * mm, "offsetDistance" : 25 * mm, "hasDraft" : true, "draftAngle" : 5 * degree, "draftPullDirection" : true});
        }
        {
            var Q0;
            {var subQ0=sQuery(id+"F4.wireOp",EDGE,"E49.MirrorCS");var subQ1=sQuery(id+"F4.wireOp",EDGE,"E21");var subQ2=makeQuery(id+"F4.imprint","INTERSECT",VERTEX,{"disambiguationData":[OD(0.0)],"derivedFrom":[subQ1,subQ0]});Q0=makeQuery(id+"F4.imprint","IMPRINT",FACE,{"disambiguationData":[TD([[makeQuery(id+"F4.imprint","IMPRINT",EDGE,{"disambiguationData":[TD([[subQ2,-1.0]])],"derivedFrom":subQ1}),-1.0]])]});}
            var Q1;
            {var subQ0=sQuery(id+"F4.wireOp",EDGE,"E49.MirrorCS");var subQ1=sQuery(id+"F4.wireOp",EDGE,"E21");var subQ2=makeQuery(id+"F4.imprint","INTERSECT",VERTEX,{"disambiguationData":[OD(0.0)],"derivedFrom":[subQ1,subQ0]});Q1=makeQuery(id+"F4.imprint","IMPRINT",FACE,{"disambiguationData":[TD([[makeQuery(id+"F4.imprint","IMPRINT",EDGE,{"disambiguationData":[TD([[subQ2,-1.0]])],"derivedFrom":subQ1}),1.0]])]});}
            var Q2;
            {var subQ0=sQuery(id+"F4.wireOp",EDGE,"E49.MirrorCS");var subQ1=sQuery(id+"F4.wireOp",EDGE,"E20");var subQ2=makeQuery(id+"F4.imprint","INTERSECT",VERTEX,{"disambiguationData":[OD(0.0)],"derivedFrom":[subQ1,subQ0]});Q2=makeQuery(id+"F4.imprint","IMPRINT",FACE,{"disambiguationData":[TD([[makeQuery(id+"F4.imprint","IMPRINT",EDGE,{"disambiguationData":[TD([[subQ2,-1.0]])],"derivedFrom":subQ1}),-1.0]])]});}
            var Q3;
            {var subQ0=sQuery(id+"F4.wireOp",EDGE,"E49.MirrorCS");var subQ1=sQuery(id+"F4.wireOp",EDGE,"E20");var subQ2=makeQuery(id+"F4.imprint","INTERSECT",VERTEX,{"disambiguationData":[OD(0.0)],"derivedFrom":[subQ1,subQ0]});Q3=makeQuery(id+"F4.imprint","IMPRINT",FACE,{"disambiguationData":[TD([[makeQuery(id+"F4.imprint","IMPRINT",EDGE,{"disambiguationData":[TD([[subQ2,-1.0]])],"derivedFrom":subQ1}),1.0]])]});}
            var Q4;
            {var subQ0=sQuery(id+"F4.wireOp",EDGE,"E48");var subQ1=sQuery(id+"F4.wireOp",EDGE,"E20");var subQ2=makeQuery(id+"F4.imprint","INTERSECT",VERTEX,{"disambiguationData":[OD(1.0)],"derivedFrom":[subQ1,subQ0]});Q4=makeQuery(id+"F4.imprint","IMPRINT",FACE,{"disambiguationData":[TD([[makeQuery(id+"F4.imprint","IMPRINT",EDGE,{"disambiguationData":[TD([[subQ2,-1.0]])],"derivedFrom":subQ1}),-1.0]])]});}
            var Q5;
            {var subQ0=sQuery(id+"F4.wireOp",EDGE,"E51.MirrorCS");var subQ1=sQuery(id+"F4.wireOp",EDGE,"E23");var subQ2=makeQuery(id+"F4.imprint","INTERSECT",VERTEX,{"disambiguationData":[OD(0.0)],"derivedFrom":[subQ1,subQ0]});Q5=makeQuery(id+"F4.imprint","IMPRINT",FACE,{"disambiguationData":[TD([[makeQuery(id+"F4.imprint","IMPRINT",EDGE,{"disambiguationData":[TD([[subQ2,-1.0]])],"derivedFrom":subQ1}),1.0]])]});}
            var Q6;
            {var subQ0=sQuery(id+"F4.wireOp",EDGE,"E50.MirrorCS");var subQ1=sQuery(id+"F4.wireOp",EDGE,"E23");var subQ2=makeQuery(id+"F4.imprint","INTERSECT",VERTEX,{"disambiguationData":[OD(1.0)],"derivedFrom":[subQ1,subQ0]});Q6=makeQuery(id+"F4.imprint","IMPRINT",FACE,{"disambiguationData":[TD([[makeQuery(id+"F4.imprint","IMPRINT",EDGE,{"disambiguationData":[TD([[subQ2,-1.0]])],"derivedFrom":subQ1}),-1.0]])]});}
            var Q7;
            {var subQ0=sQuery(id+"F4.wireOp",EDGE,"E48");var subQ1=sQuery(id+"F4.wireOp",EDGE,"E42");var subQ2=makeQuery(id+"F4.imprint","INTERSECT",VERTEX,{"derivedFrom":[subQ1,subQ0]});Q7=makeQuery(id+"F4.imprint","IMPRINT",FACE,{"disambiguationData":[TD([[makeQuery(id+"F4.imprint","IMPRINT",EDGE,{"disambiguationData":[TD([[subQ2,-1.0]])],"derivedFrom":subQ1}),1.0]])]});}
            var Q8;
            {var subQ0=sQuery(id+"F4.wireOp",EDGE,"E50.MirrorCS");var subQ1=sQuery(id+"F4.wireOp",EDGE,"E43");var subQ2=makeQuery(id+"F4.imprint","INTERSECT",VERTEX,{"derivedFrom":[subQ1,subQ0]});Q8=makeQuery(id+"F4.imprint","IMPRINT",FACE,{"disambiguationData":[TD([[makeQuery(id+"F4.imprint","IMPRINT",EDGE,{"disambiguationData":[TD([[subQ2,-1.0]])],"derivedFrom":subQ1}),1.0]])]});}
            var Q9;
            {var subQ0=sQuery(id+"F4.wireOp",EDGE,"E50.MirrorCS");var subQ1=sQuery(id+"F4.wireOp",EDGE,"E22");var subQ2=makeQuery(id+"F4.imprint","INTERSECT",VERTEX,{"disambiguationData":[OD(1.0)],"derivedFrom":[subQ1,subQ0]});Q9=makeQuery(id+"F4.imprint","IMPRINT",FACE,{"disambiguationData":[TD([[makeQuery(id+"F4.imprint","IMPRINT",EDGE,{"disambiguationData":[TD([[subQ2,-1.0]])],"derivedFrom":subQ1}),-1.0]])]});}
            var Q10;
            {var subQ0=sQuery(id+"F4.wireOp",EDGE,"E51.MirrorCS");var subQ1=sQuery(id+"F4.wireOp",EDGE,"E22");var subQ2=makeQuery(id+"F4.imprint","INTERSECT",VERTEX,{"disambiguationData":[OD(0.0)],"derivedFrom":[subQ1,subQ0]});Q10=makeQuery(id+"F4.imprint","IMPRINT",FACE,{"disambiguationData":[TD([[makeQuery(id+"F4.imprint","IMPRINT",EDGE,{"disambiguationData":[TD([[subQ2,-1.0]])],"derivedFrom":subQ1}),1.0]])]});}
            var Q11;
            {var subQ0=sQuery(id+"F4.wireOp",EDGE,"E48");var subQ1=sQuery(id+"F4.wireOp",EDGE,"E40");var subQ2=makeQuery(id+"F4.imprint","INTERSECT",VERTEX,{"derivedFrom":[subQ1,subQ0]});Q11=makeQuery(id+"F4.imprint","IMPRINT",FACE,{"disambiguationData":[TD([[makeQuery(id+"F4.imprint","IMPRINT",EDGE,{"disambiguationData":[TD([[subQ2,-1.0]])],"derivedFrom":subQ1}),-1.0]])]});}
            var Q12;
            {var subQ0=sQuery(id+"F4.wireOp",EDGE,"E50.MirrorCS");var subQ1=sQuery(id+"F4.wireOp",EDGE,"E41");var subQ2=makeQuery(id+"F4.imprint","INTERSECT",VERTEX,{"derivedFrom":[subQ1,subQ0]});Q12=makeQuery(id+"F4.imprint","IMPRINT",FACE,{"disambiguationData":[TD([[makeQuery(id+"F4.imprint","IMPRINT",EDGE,{"disambiguationData":[TD([[subQ2,-1.0]])],"derivedFrom":subQ1}),-1.0]])]});}
            var Q13;
            {var subQ0=sQuery(id+"F4.wireOp",EDGE,"E51.MirrorCS");var subQ1=sQuery(id+"F4.wireOp",EDGE,"E22");var subQ2=makeQuery(id+"F4.imprint","INTERSECT",VERTEX,{"disambiguationData":[OD(0.0)],"derivedFrom":[subQ1,subQ0]});Q13=makeQuery(id+"F4.imprint","IMPRINT",FACE,{"disambiguationData":[TD([[makeQuery(id+"F4.imprint","IMPRINT",EDGE,{"disambiguationData":[TD([[subQ2,-1.0]])],"derivedFrom":subQ1}),-1.0]])]});}
            extrude(context, id + "F6", {"entities" : qUnion([Q0, Q1, Q2, Q3, Q4, Q5, Q6, Q7, Q8, Q9, Q10, Q11, Q12, Q13]), "operationType" : NewBodyOperationType.REMOVE, "oppositeDirection" : true, "depth" : 8 * mm, "offsetDistance" : 25 * mm, "hasDraft" : true, "draftAngle" : 5 * degree, "draftPullDirection" : true});
        }
        {
            var Q0;
            Q0=makeQuery(id+"F1.opExtrude","SWEPT_EDGE",EDGE,{"disambiguationData":[OSD([sQuery(id+"F0.wireOp",EDGE,"E8.top"),sQuery(id+"F0.wireOp",EDGE,"E8.left")])]});
            var Q1;
            Q1=makeQuery(id+"F1.opExtrude","SWEPT_EDGE",EDGE,{"disambiguationData":[OSD([sQuery(id+"F0.wireOp",EDGE,"E8.top"),sQuery(id+"F0.wireOp",EDGE,"E8.right")])]});
            var Q2;
            Q2=makeQuery(id+"F1.opExtrude","SWEPT_EDGE",EDGE,{"disambiguationData":[OSD([sQuery(id+"F0.wireOp",EDGE,"E8.bottom"),sQuery(id+"F0.wireOp",EDGE,"E8.right")])]});
            var Q3;
            Q3=makeQuery(id+"F1.opExtrude","SWEPT_EDGE",EDGE,{"disambiguationData":[OSD([sQuery(id+"F0.wireOp",EDGE,"E8.bottom"),sQuery(id+"F0.wireOp",EDGE,"E8.left")])]});
            fillet(context, id + "F7", {"entities" : qUnion([Q0, Q1, Q2, Q3]), "radius" : 25 * mm, "tangentPropagation" : true, "allowEdgeOverflow" : false});
        }
        {
            var Q0;
            Q0=makeQuery(id+"F3.opExtrude","SWEPT_EDGE",EDGE,{"disambiguationData":[OSD([sQuery(id+"F2.wireOp",EDGE,"E13.bottom"),sQuery(id+"F2.wireOp",EDGE,"E13.right")])]});
            var Q1;
            Q1=makeQuery(id+"F3.opExtrude","SWEPT_EDGE",EDGE,{"disambiguationData":[OSD([sQuery(id+"F2.wireOp",EDGE,"E13.top"),sQuery(id+"F2.wireOp",EDGE,"E13.right")])]});
            var Q2;
            Q2=makeQuery(id+"F3.opExtrude","SWEPT_EDGE",EDGE,{"disambiguationData":[OSD([sQuery(id+"F2.wireOp",EDGE,"E13.top"),sQuery(id+"F2.wireOp",EDGE,"E13.left")])]});
            var Q3;
            Q3=makeQuery(id+"F3.opExtrude","SWEPT_EDGE",EDGE,{"disambiguationData":[OSD([sQuery(id+"F2.wireOp",EDGE,"E13.bottom"),sQuery(id+"F2.wireOp",EDGE,"E13.left")])]});
            fillet(context, id + "F8", {"entities" : qUnion([Q0, Q1, Q2, Q3]), "radius" : 25 * mm, "tangentPropagation" : true, "allowEdgeOverflow" : false});
        }
        {
            var Q0;
            {var subQ0=sQuery(id+"F0.wireOp",EDGE,"E8.top");Q0=makeQuery(id+"F5.boolean.opBoolean","SPLIT",EDGE,{"disambiguationData":[TD([makeQuery(id+"F5.opExtrude","SWEPT_FACE",FACE,{"disambiguationData":[OSD([sQuery(id+"F4.wireOp",EDGE,"E36.MirrorCS"),sQuery(id+"F4.wireOp",EDGE,"E45.MirrorCS")])]})])],"derivedFrom":makeQuery(id+"F1.opExtrude","CAP_EDGE",EDGE,{"disambiguationData":[OSD([subQ0])],"isStart":true})});}
            var Q1;
            {var subQ0=sQuery(id+"F0.wireOp",EDGE,"E8.right");var subQ1=sQuery(id+"F0.wireOp",EDGE,"E8.top");Q1=makeQuery(id+"F5.boolean.opBoolean","SPLIT",EDGE,{"disambiguationData":[TD([makeQuery(id+"F1.opExtrude","SWEPT_FACE",FACE,{"disambiguationData":[OSD([subQ0])]})])],"derivedFrom":makeQuery(id+"F1.opExtrude","CAP_EDGE",EDGE,{"disambiguationData":[OSD([subQ1])],"isStart":true})});}
            var Q2;
            Q2=makeQuery(id+"F1.opExtrude","CAP_EDGE",EDGE,{"disambiguationData":[OSD([sQuery(id+"F0.wireOp",EDGE,"E8.left")])],"isStart":true});
            var Q3;
            {var subQ0=sQuery(id+"F0.wireOp",EDGE,"E8.bottom");Q3=makeQuery(id+"F5.boolean.opBoolean","SPLIT",EDGE,{"disambiguationData":[TD([makeQuery(id+"F5.opExtrude","SWEPT_FACE",FACE,{"disambiguationData":[OSD([sQuery(id+"F4.wireOp",EDGE,"E33.MirrorCS"),sQuery(id+"F4.wireOp",EDGE,"E46.MirrorCS")])]})])],"derivedFrom":makeQuery(id+"F1.opExtrude","CAP_EDGE",EDGE,{"disambiguationData":[OSD([subQ0])],"isStart":true})});}
            var Q4;
            {var subQ0=makeQuery(id+"F1.opExtrude","SWEPT_FACE",FACE,{"disambiguationData":[OSD([sQuery(id+"F0.wireOp",EDGE,"E8.bottom")])]});var subQ1=sQuery(id+"F4.wireOp",EDGE,"E45.MirrorCS");var subQ2=sQuery(id+"F4.wireOp",EDGE,"E34.MirrorCS");var subQ3=makeQuery(id+"F5.opExtrude","CAP_FACE",FACE,{"disambiguationData":[OSD([sQuery(id+"F4.wireOp",EDGE,"E20"),sQuery(id+"F4.wireOp",EDGE,"E21"),subQ2,sQuery(id+"F4.wireOp",EDGE,"E35.MirrorCS"),sQuery(id+"F4.wireOp",EDGE,"E36.MirrorCS"),sQuery(id+"F4.wireOp",EDGE,"E37.MirrorCS"),sQuery(id+"F4.wireOp",EDGE,"E40"),sQuery(id+"F4.wireOp",EDGE,"E42"),sQuery(id+"F4.wireOp",EDGE,"E44"),subQ1])],"isStart":false});Q4=makeQuery(id+"F6.boolean.opBoolean","SPLIT",EDGE,{"disambiguationData":[TD([makeQuery(id+"F6.opExtrude","SWEPT_FACE",FACE,{"disambiguationData":[OSD([sQuery(id+"F4.wireOp",EDGE,"E49.MirrorCS")])]})])],"derivedFrom":makeQuery(id+"F5.boolean.opBoolean","INTERSECT",EDGE,{"derivedFrom":[subQ0,subQ3]})});}
            var Q5;
            {var subQ0=makeQuery(id+"F1.opExtrude","SWEPT_FACE",FACE,{"disambiguationData":[OSD([sQuery(id+"F0.wireOp",EDGE,"E8.bottom")])]});var subQ1=sQuery(id+"F4.wireOp",EDGE,"E44");var subQ2=sQuery(id+"F4.wireOp",EDGE,"E35.MirrorCS");var subQ3=makeQuery(id+"F5.opExtrude","CAP_FACE",FACE,{"disambiguationData":[OSD([sQuery(id+"F4.wireOp",EDGE,"E20"),sQuery(id+"F4.wireOp",EDGE,"E21"),sQuery(id+"F4.wireOp",EDGE,"E34.MirrorCS"),subQ2,sQuery(id+"F4.wireOp",EDGE,"E36.MirrorCS"),sQuery(id+"F4.wireOp",EDGE,"E37.MirrorCS"),sQuery(id+"F4.wireOp",EDGE,"E40"),sQuery(id+"F4.wireOp",EDGE,"E42"),subQ1,sQuery(id+"F4.wireOp",EDGE,"E45.MirrorCS")])],"isStart":false});Q5=makeQuery(id+"F6.boolean.opBoolean","SPLIT",EDGE,{"disambiguationData":[TD([makeQuery(id+"F6.opExtrude","SWEPT_FACE",FACE,{"disambiguationData":[OSD([sQuery(id+"F4.wireOp",EDGE,"E48")])]})])],"derivedFrom":makeQuery(id+"F5.boolean.opBoolean","INTERSECT",EDGE,{"derivedFrom":[subQ0,subQ3]})});}
            var Q6;
            {var subQ0=makeQuery(id+"F1.opExtrude","SWEPT_FACE",FACE,{"disambiguationData":[OSD([sQuery(id+"F0.wireOp",EDGE,"E8.bottom")])]});var subQ1=sQuery(id+"F4.wireOp",EDGE,"E46.MirrorCS");var subQ2=sQuery(id+"F4.wireOp",EDGE,"E33.MirrorCS");var subQ3=makeQuery(id+"F5.opExtrude","CAP_FACE",FACE,{"disambiguationData":[OSD([sQuery(id+"F4.wireOp",EDGE,"E22"),sQuery(id+"F4.wireOp",EDGE,"E23"),sQuery(id+"F4.wireOp",EDGE,"E24"),subQ2,sQuery(id+"F4.wireOp",EDGE,"E38.MirrorCS"),sQuery(id+"F4.wireOp",EDGE,"E39.MirrorCS"),sQuery(id+"F4.wireOp",EDGE,"E41"),sQuery(id+"F4.wireOp",EDGE,"E43"),subQ1,sQuery(id+"F4.wireOp",EDGE,"E47.MirrorCS")])],"isStart":false});Q6=makeQuery(id+"F6.boolean.opBoolean","SPLIT",EDGE,{"disambiguationData":[TD([makeQuery(id+"F6.opExtrude","SWEPT_FACE",FACE,{"disambiguationData":[OSD([sQuery(id+"F4.wireOp",EDGE,"E50.MirrorCS")])]})])],"derivedFrom":makeQuery(id+"F5.boolean.opBoolean","INTERSECT",EDGE,{"derivedFrom":[subQ0,subQ3]})});}
            var Q7;
            {var subQ0=makeQuery(id+"F1.opExtrude","SWEPT_FACE",FACE,{"disambiguationData":[OSD([sQuery(id+"F0.wireOp",EDGE,"E8.bottom")])]});var subQ1=sQuery(id+"F4.wireOp",EDGE,"E47.MirrorCS");var subQ2=sQuery(id+"F4.wireOp",EDGE,"E24");var subQ3=makeQuery(id+"F5.opExtrude","CAP_FACE",FACE,{"disambiguationData":[OSD([sQuery(id+"F4.wireOp",EDGE,"E22"),sQuery(id+"F4.wireOp",EDGE,"E23"),subQ2,sQuery(id+"F4.wireOp",EDGE,"E33.MirrorCS"),sQuery(id+"F4.wireOp",EDGE,"E38.MirrorCS"),sQuery(id+"F4.wireOp",EDGE,"E39.MirrorCS"),sQuery(id+"F4.wireOp",EDGE,"E41"),sQuery(id+"F4.wireOp",EDGE,"E43"),sQuery(id+"F4.wireOp",EDGE,"E46.MirrorCS"),subQ1])],"isStart":false});Q7=makeQuery(id+"F6.boolean.opBoolean","SPLIT",EDGE,{"disambiguationData":[TD([makeQuery(id+"F6.opExtrude","SWEPT_FACE",FACE,{"disambiguationData":[OSD([sQuery(id+"F4.wireOp",EDGE,"E51.MirrorCS")])]})])],"derivedFrom":makeQuery(id+"F5.boolean.opBoolean","INTERSECT",EDGE,{"derivedFrom":[subQ0,subQ3]})});}
            var Q8;
            {var subQ0=makeQuery(id+"F1.opExtrude","SWEPT_FACE",FACE,{"disambiguationData":[OSD([sQuery(id+"F0.wireOp",EDGE,"E8.top")])]});var subQ1=sQuery(id+"F4.wireOp",EDGE,"E44");var subQ2=sQuery(id+"F4.wireOp",EDGE,"E37.MirrorCS");var subQ3=makeQuery(id+"F5.opExtrude","CAP_FACE",FACE,{"disambiguationData":[OSD([sQuery(id+"F4.wireOp",EDGE,"E20"),sQuery(id+"F4.wireOp",EDGE,"E21"),sQuery(id+"F4.wireOp",EDGE,"E34.MirrorCS"),sQuery(id+"F4.wireOp",EDGE,"E35.MirrorCS"),sQuery(id+"F4.wireOp",EDGE,"E36.MirrorCS"),subQ2,sQuery(id+"F4.wireOp",EDGE,"E40"),sQuery(id+"F4.wireOp",EDGE,"E42"),subQ1,sQuery(id+"F4.wireOp",EDGE,"E45.MirrorCS")])],"isStart":false});Q8=makeQuery(id+"F6.boolean.opBoolean","SPLIT",EDGE,{"disambiguationData":[TD([makeQuery(id+"F6.opExtrude","SWEPT_FACE",FACE,{"disambiguationData":[OSD([sQuery(id+"F4.wireOp",EDGE,"E48")])]})])],"derivedFrom":makeQuery(id+"F5.boolean.opBoolean","INTERSECT",EDGE,{"derivedFrom":[subQ0,subQ3]})});}
            var Q9;
            {var subQ0=makeQuery(id+"F1.opExtrude","SWEPT_FACE",FACE,{"disambiguationData":[OSD([sQuery(id+"F0.wireOp",EDGE,"E8.top")])]});var subQ1=sQuery(id+"F4.wireOp",EDGE,"E45.MirrorCS");var subQ2=sQuery(id+"F4.wireOp",EDGE,"E36.MirrorCS");var subQ3=makeQuery(id+"F5.opExtrude","CAP_FACE",FACE,{"disambiguationData":[OSD([sQuery(id+"F4.wireOp",EDGE,"E20"),sQuery(id+"F4.wireOp",EDGE,"E21"),sQuery(id+"F4.wireOp",EDGE,"E34.MirrorCS"),sQuery(id+"F4.wireOp",EDGE,"E35.MirrorCS"),subQ2,sQuery(id+"F4.wireOp",EDGE,"E37.MirrorCS"),sQuery(id+"F4.wireOp",EDGE,"E40"),sQuery(id+"F4.wireOp",EDGE,"E42"),sQuery(id+"F4.wireOp",EDGE,"E44"),subQ1])],"isStart":false});Q9=makeQuery(id+"F6.boolean.opBoolean","SPLIT",EDGE,{"disambiguationData":[TD([makeQuery(id+"F6.opExtrude","SWEPT_FACE",FACE,{"disambiguationData":[OSD([sQuery(id+"F4.wireOp",EDGE,"E49.MirrorCS")])]})])],"derivedFrom":makeQuery(id+"F5.boolean.opBoolean","INTERSECT",EDGE,{"derivedFrom":[subQ0,subQ3]})});}
            var Q10;
            {var subQ0=makeQuery(id+"F1.opExtrude","SWEPT_FACE",FACE,{"disambiguationData":[OSD([sQuery(id+"F0.wireOp",EDGE,"E8.top")])]});var subQ1=sQuery(id+"F4.wireOp",EDGE,"E46.MirrorCS");var subQ2=sQuery(id+"F4.wireOp",EDGE,"E38.MirrorCS");var subQ3=makeQuery(id+"F5.opExtrude","CAP_FACE",FACE,{"disambiguationData":[OSD([sQuery(id+"F4.wireOp",EDGE,"E22"),sQuery(id+"F4.wireOp",EDGE,"E23"),sQuery(id+"F4.wireOp",EDGE,"E24"),sQuery(id+"F4.wireOp",EDGE,"E33.MirrorCS"),subQ2,sQuery(id+"F4.wireOp",EDGE,"E39.MirrorCS"),sQuery(id+"F4.wireOp",EDGE,"E41"),sQuery(id+"F4.wireOp",EDGE,"E43"),subQ1,sQuery(id+"F4.wireOp",EDGE,"E47.MirrorCS")])],"isStart":false});Q10=makeQuery(id+"F6.boolean.opBoolean","SPLIT",EDGE,{"disambiguationData":[TD([makeQuery(id+"F6.opExtrude","SWEPT_FACE",FACE,{"disambiguationData":[OSD([sQuery(id+"F4.wireOp",EDGE,"E50.MirrorCS")])]})])],"derivedFrom":makeQuery(id+"F5.boolean.opBoolean","INTERSECT",EDGE,{"derivedFrom":[subQ0,subQ3]})});}
            var Q11;
            {var subQ0=makeQuery(id+"F1.opExtrude","SWEPT_FACE",FACE,{"disambiguationData":[OSD([sQuery(id+"F0.wireOp",EDGE,"E8.top")])]});var subQ1=sQuery(id+"F4.wireOp",EDGE,"E47.MirrorCS");var subQ2=sQuery(id+"F4.wireOp",EDGE,"E39.MirrorCS");var subQ3=makeQuery(id+"F5.opExtrude","CAP_FACE",FACE,{"disambiguationData":[OSD([sQuery(id+"F4.wireOp",EDGE,"E22"),sQuery(id+"F4.wireOp",EDGE,"E23"),sQuery(id+"F4.wireOp",EDGE,"E24"),sQuery(id+"F4.wireOp",EDGE,"E33.MirrorCS"),sQuery(id+"F4.wireOp",EDGE,"E38.MirrorCS"),subQ2,sQuery(id+"F4.wireOp",EDGE,"E41"),sQuery(id+"F4.wireOp",EDGE,"E43"),sQuery(id+"F4.wireOp",EDGE,"E46.MirrorCS"),subQ1])],"isStart":false});Q11=makeQuery(id+"F6.boolean.opBoolean","SPLIT",EDGE,{"disambiguationData":[TD([makeQuery(id+"F6.opExtrude","SWEPT_FACE",FACE,{"disambiguationData":[OSD([sQuery(id+"F4.wireOp",EDGE,"E51.MirrorCS")])]})])],"derivedFrom":makeQuery(id+"F5.boolean.opBoolean","INTERSECT",EDGE,{"derivedFrom":[subQ0,subQ3]})});}
            fillet(context, id + "F9", {"entities" : qUnion([Q0, Q1, Q2, Q3, Q4, Q5, Q6, Q7, Q8, Q9, Q10, Q11]), "radius" : 1.5 * mm, "tangentPropagation" : true, "allowEdgeOverflow" : false});
        }
        {
            var Q0;
            Q0=makeQuery(id+"F3.opExtrude","CAP_FACE",FACE,{"disambiguationData":[OSD([sQuery(id+"F2.wireOp",EDGE,"E13.bottom"),sQuery(id+"F2.wireOp",EDGE,"E13.top"),sQuery(id+"F2.wireOp",EDGE,"E13.left"),sQuery(id+"F2.wireOp",EDGE,"E13.right")])],"isStart":false});
            shell(context, id + "F10", {"entities" : qUnion([Q0]), "thickness" : 3 * mm});
        }
        {
            var Q0;
            Q0=makeQuery(id+"FFMxlwrzM48GTUP_1.boolean.opBoolean","MERGE",FACE,{"derivedFrom":[makeQuery(id+"F3.opExtrude","CAP_FACE",FACE,{"disambiguationData":[OSD([sQuery(id+"F2.wireOp",EDGE,"E13.bottom"),sQuery(id+"F2.wireOp",EDGE,"E13.top"),sQuery(id+"F2.wireOp",EDGE,"E13.left"),sQuery(id+"F2.wireOp",EDGE,"E13.right")])],"isStart":true}),makeQuery(id+"FFMxlwrzM48GTUP_1.opExtrude","CAP_FACE",FACE,{"disambiguationData":[OSD([sQuery(id+"F4.wireOp",EDGE,"E24"),sQuery(id+"F4.wireOp",EDGE,"0tpGAXtC-clnW-DzUJ-E4Gk-3UYplvxCWuQU"),sQuery(id+"F4.wireOp",EDGE,"E33.MirrorCS"),sQuery(id+"F4.wireOp",EDGE,"E41")])],"isStart":false}),makeQuery(id+"FFMxlwrzM48GTUP_1.opExtrude","CAP_FACE",FACE,{"disambiguationData":[OSD([sQuery(id+"F4.wireOp",EDGE,"6fd3e808-e90c-4549-8836-5e467082efef0.MirrorCS"),sQuery(id+"F4.wireOp",EDGE,"E34.MirrorCS"),sQuery(id+"F4.wireOp",EDGE,"E35.MirrorCS"),sQuery(id+"F4.wireOp",EDGE,"E40")])],"isStart":false}),makeQuery(id+"FFMxlwrzM48GTUP_1.opExtrude","CAP_FACE",FACE,{"disambiguationData":[OSD([sQuery(id+"F4.wireOp",EDGE,"e49ff9fc-5064-4601-90bc-e5e2885164bb0.MirrorCS"),sQuery(id+"F4.wireOp",EDGE,"E36.MirrorCS"),sQuery(id+"F4.wireOp",EDGE,"E37.MirrorCS"),sQuery(id+"F4.wireOp",EDGE,"E42")])],"isStart":false}),makeQuery(id+"FFMxlwrzM48GTUP_1.opExtrude","CAP_FACE",FACE,{"disambiguationData":[OSD([sQuery(id+"F4.wireOp",EDGE,"446428ba-9815-4af7-82a4-81c271596e950.MirrorCS"),sQuery(id+"F4.wireOp",EDGE,"E38.MirrorCS"),sQuery(id+"F4.wireOp",EDGE,"E39.MirrorCS"),sQuery(id+"F4.wireOp",EDGE,"E43")])],"isStart":false})]});
            var sketch = newSketch(context, id + "F11", { "sketchPlane" : qUnion([Q0])});
            skLineSegment(sketch, "E52", {"start": v(-111.2, 0) * mm, "end": v(-209.56, 0) * mm, "construction": true});
            skLineSegment(sketch, "E53", {"start": v(-111.2, 40) * mm, "end": v(-117.2, 40) * mm});
            skLineSegment(sketch, "E54.MirrorCS", {"start": v(-111.2, -40) * mm, "end": v(-117.2, -40) * mm});
            skLineSegment(sketch, "E55", {"start": v(-117.2, 40) * mm, "end": v(-117.2, -40) * mm});
            skLineSegment(sketch, "E56.MirrorCS", {"start": v(117.2, 40) * mm, "end": v(117.2, -40) * mm});
            skLineSegment(sketch, "E57.MirrorCS", {"start": v(111.2, 40) * mm, "end": v(117.2, 40) * mm});
            skLineSegment(sketch, "E58.MirrorCS", {"start": v(111.2, -40) * mm, "end": v(117.2, -40) * mm});
            skLineSegment(sketch, "E59", {"start": v(0, 0) * mm, "end": v(0, 134.49) * mm, "construction": true});
            skLineSegment(sketch, "E60", {"start": v(-37.04, 110.14) * mm, "end": v(-37.04, 116.14) * mm});
            skLineSegment(sketch, "E61", {"start": v(-37.04, 116.14) * mm, "end": v(42.96, 116.14) * mm});
            skLineSegment(sketch, "E62", {"start": v(42.96, 116.14) * mm, "end": v(42.96, 110.14) * mm});
            skLineSegment(sketch, "E63.MirrorCS", {"start": v(-37.04, -116.14) * mm, "end": v(42.96, -116.14) * mm});
            skLineSegment(sketch, "E64.MirrorCS", {"start": v(-37.04, -110.14) * mm, "end": v(-37.04, -116.14) * mm});
            skLineSegment(sketch, "E65.MirrorCS", {"start": v(42.96, -116.14) * mm, "end": v(42.96, -110.14) * mm});
            skSolve(sketch);
        }
        {
            var Q0;
            {var subQ0=sQuery(id+"F11.wireOp",EDGE,"E53");Q0=makeQuery(id+"F11.imprint","IMPRINT",FACE,{"disambiguationData":[TD([[makeQuery(id+"F11.imprint","IMPRINT",EDGE,{"derivedFrom":subQ0}),1.0]])]});}
            var Q1;
            Q1=makeQuery(id+"F11.imprint","IMPRINT",FACE,{"disambiguationData":[TD([[makeQuery(id+"F11.imprint","IMPRINT",EDGE,{"derivedFrom":sQuery(id+"F11.wireOp",EDGE,"E56.MirrorCS")}),-1.0]])]});
            var Q2;
            {var subQ0=sQuery(id+"F11.wireOp",EDGE,"E61");Q2=makeQuery(id+"F11.imprint","IMPRINT",FACE,{"disambiguationData":[TD([[makeQuery(id+"F11.imprint","IMPRINT",EDGE,{"derivedFrom":subQ0}),-1.0]])]});}
            var Q3;
            {var subQ0=sQuery(id+"F11.wireOp",EDGE,"E63.MirrorCS");Q3=makeQuery(id+"F11.imprint","IMPRINT",FACE,{"disambiguationData":[TD([[makeQuery(id+"F11.imprint","IMPRINT",EDGE,{"derivedFrom":subQ0}),1.0]])]});}
            extrude(context, id + "F12", {"entities" : qUnion([Q0, Q1, Q2, Q3]), "operationType" : NewBodyOperationType.ADD, "oppositeDirection" : true, "depth" : 3 * mm, "offsetDistance" : 25 * mm, "hasDraft" : true, "draftAngle" : 6 * degree});
        }
        {
            var Q0;
            Q0=makeQuery(id+"F12.boolean.opBoolean","INTERSECT",EDGE,{"derivedFrom":[makeQuery(id+"F3.opExtrude","SWEPT_FACE",FACE,{"disambiguationData":[OSD([sQuery(id+"F2.wireOp",EDGE,"E13.left")])]}),makeQuery(id+"F12.opExtrude","SWEPT_FACE",FACE,{"disambiguationData":[OSD([sQuery(id+"F11.wireOp",EDGE,"E54.MirrorCS")])]})]});
            var Q1;
            Q1=makeQuery(id+"F12.boolean.opBoolean","INTERSECT",EDGE,{"derivedFrom":[makeQuery(id+"F3.opExtrude","SWEPT_FACE",FACE,{"disambiguationData":[OSD([sQuery(id+"F2.wireOp",EDGE,"E13.left")])]}),makeQuery(id+"F12.opExtrude","SWEPT_FACE",FACE,{"disambiguationData":[OSD([sQuery(id+"F11.wireOp",EDGE,"E53")])]})]});
            var Q2;
            Q2=makeQuery(id+"F12.opExtrude","SWEPT_EDGE",EDGE,{"disambiguationData":[OSD([sQuery(id+"F11.wireOp",EDGE,"E53"),sQuery(id+"F11.wireOp",EDGE,"E55")])]});
            var Q3;
            Q3=makeQuery(id+"F12.opExtrude","SWEPT_EDGE",EDGE,{"disambiguationData":[OSD([sQuery(id+"F11.wireOp",EDGE,"E54.MirrorCS"),sQuery(id+"F11.wireOp",EDGE,"E55")])]});
            var Q4;
            Q4=makeQuery(id+"F12.opExtrude","SWEPT_EDGE",EDGE,{"disambiguationData":[OSD([sQuery(id+"F11.wireOp",EDGE,"E56.MirrorCS"),sQuery(id+"F11.wireOp",EDGE,"E58.MirrorCS")])]});
            var Q5;
            Q5=makeQuery(id+"F12.boolean.opBoolean","INTERSECT",EDGE,{"derivedFrom":[makeQuery(id+"F3.opExtrude","SWEPT_FACE",FACE,{"disambiguationData":[OSD([sQuery(id+"F2.wireOp",EDGE,"E13.right")])]}),makeQuery(id+"F12.opExtrude","SWEPT_FACE",FACE,{"disambiguationData":[OSD([sQuery(id+"F11.wireOp",EDGE,"E58.MirrorCS")])]})]});
            var Q6;
            Q6=makeQuery(id+"F12.boolean.opBoolean","INTERSECT",EDGE,{"derivedFrom":[makeQuery(id+"F3.opExtrude","SWEPT_FACE",FACE,{"disambiguationData":[OSD([sQuery(id+"F2.wireOp",EDGE,"E13.right")])]}),makeQuery(id+"F12.opExtrude","SWEPT_FACE",FACE,{"disambiguationData":[OSD([sQuery(id+"F11.wireOp",EDGE,"E57.MirrorCS")])]})]});
            var Q7;
            Q7=makeQuery(id+"F12.opExtrude","SWEPT_EDGE",EDGE,{"disambiguationData":[OSD([sQuery(id+"F11.wireOp",EDGE,"E56.MirrorCS"),sQuery(id+"F11.wireOp",EDGE,"E57.MirrorCS")])]});
            var Q8;
            Q8=makeQuery(id+"F12.boolean.opBoolean","INTERSECT",EDGE,{"derivedFrom":[makeQuery(id+"F3.opExtrude","SWEPT_FACE",FACE,{"disambiguationData":[OSD([sQuery(id+"F2.wireOp",EDGE,"E13.bottom")])]}),makeQuery(id+"F12.opExtrude","SWEPT_FACE",FACE,{"disambiguationData":[OSD([sQuery(id+"F11.wireOp",EDGE,"E64.MirrorCS")])]})]});
            var Q9;
            Q9=makeQuery(id+"F12.opExtrude","SWEPT_EDGE",EDGE,{"disambiguationData":[OSD([sQuery(id+"F11.wireOp",EDGE,"E63.MirrorCS"),sQuery(id+"F11.wireOp",EDGE,"E64.MirrorCS")])]});
            var Q10;
            Q10=makeQuery(id+"F12.opExtrude","SWEPT_EDGE",EDGE,{"disambiguationData":[OSD([sQuery(id+"F11.wireOp",EDGE,"E63.MirrorCS"),sQuery(id+"F11.wireOp",EDGE,"E65.MirrorCS")])]});
            var Q11;
            Q11=makeQuery(id+"F12.boolean.opBoolean","INTERSECT",EDGE,{"derivedFrom":[makeQuery(id+"F3.opExtrude","SWEPT_FACE",FACE,{"disambiguationData":[OSD([sQuery(id+"F2.wireOp",EDGE,"E13.bottom")])]}),makeQuery(id+"F12.opExtrude","SWEPT_FACE",FACE,{"disambiguationData":[OSD([sQuery(id+"F11.wireOp",EDGE,"E65.MirrorCS")])]})]});
            var Q12;
            Q12=makeQuery(id+"F12.boolean.opBoolean","INTERSECT",EDGE,{"derivedFrom":[makeQuery(id+"F3.opExtrude","SWEPT_FACE",FACE,{"disambiguationData":[OSD([sQuery(id+"F2.wireOp",EDGE,"E13.top")])]}),makeQuery(id+"F12.opExtrude","SWEPT_FACE",FACE,{"disambiguationData":[OSD([sQuery(id+"F11.wireOp",EDGE,"E62")])]})]});
            var Q13;
            Q13=makeQuery(id+"F12.opExtrude","SWEPT_EDGE",EDGE,{"disambiguationData":[OSD([sQuery(id+"F11.wireOp",EDGE,"E61"),sQuery(id+"F11.wireOp",EDGE,"E62")])]});
            var Q14;
            Q14=makeQuery(id+"F12.opExtrude","SWEPT_EDGE",EDGE,{"disambiguationData":[OSD([sQuery(id+"F11.wireOp",EDGE,"E60"),sQuery(id+"F11.wireOp",EDGE,"E61")])]});
            var Q15;
            Q15=makeQuery(id+"F12.boolean.opBoolean","INTERSECT",EDGE,{"derivedFrom":[makeQuery(id+"F3.opExtrude","SWEPT_FACE",FACE,{"disambiguationData":[OSD([sQuery(id+"F2.wireOp",EDGE,"E13.top")])]}),makeQuery(id+"F12.opExtrude","SWEPT_FACE",FACE,{"disambiguationData":[OSD([sQuery(id+"F11.wireOp",EDGE,"E60")])]})]});
            fillet(context, id + "F13", {"entities" : qUnion([Q0, Q1, Q2, Q3, Q4, Q5, Q6, Q7, Q8, Q9, Q10, Q11, Q12, Q13, Q14, Q15]), "radius" : 2 * mm, "tangentPropagation" : true, "allowEdgeOverflow" : false});
        }
        {
            var Q0;
            Q0=makeQuery(id+"F12.opExtrude","CAP_FACE",FACE,{"disambiguationData":[OSD([sQuery(id+"F4.wireOp",EDGE,"E40"),sQuery(id+"F4.wireOp",EDGE,"E41"),sQuery(id+"F4.wireOp",EDGE,"E42"),sQuery(id+"F4.wireOp",EDGE,"E43"),sQuery(id+"F4.wireOp",EDGE,"E48"),sQuery(id+"F4.wireOp",EDGE,"E49.MirrorCS"),sQuery(id+"F4.wireOp",EDGE,"E50.MirrorCS"),sQuery(id+"F4.wireOp",EDGE,"E51.MirrorCS"),sQuery(id+"F11.wireOp",EDGE,"E63.MirrorCS"),sQuery(id+"F11.wireOp",EDGE,"E64.MirrorCS"),sQuery(id+"F11.wireOp",EDGE,"E65.MirrorCS")])],"isStart":false});
            var sketch = newSketch(context, id + "F14", { "sketchPlane" : qUnion([Q0])});
            skPoint(sketch, "E66", {"position": v(-39.35, 111.46) * mm});
            skPoint(sketch, "E67", {"position": v(45.27, 111.46) * mm});
            skPoint(sketch, "E68", {"position": v(2.96, 116.46) * mm});
            skLineSegment(sketch, "E69", {"start": v(-39.35, 111.46) * mm, "end": v(-39.35, 126.46) * mm, "construction": true});
            skLineSegment(sketch, "E70", {"start": v(45.27, 111.46) * mm, "end": v(45.27, 126.46) * mm, "construction": true});
            skLineSegment(sketch, "E71.bottom", {"start": v(-39.35, 111.46) * mm, "end": v(45.27, 111.46) * mm});
            skLineSegment(sketch, "E71.top", {"start": v(-39.35, 126.46) * mm, "end": v(45.27, 126.46) * mm});
            skLineSegment(sketch, "E71.left", {"start": v(-39.35, 111.46) * mm, "end": v(-39.35, 126.46) * mm});
            skLineSegment(sketch, "E71.right", {"start": v(45.27, 111.46) * mm, "end": v(45.27, 126.46) * mm});
            skLineSegment(sketch, "E72", {"start": v(0, 0) * mm, "end": v(174.99, 0) * mm, "construction": true});
            skLineSegment(sketch, "E73.MirrorCS", {"start": v(45.27, -111.46) * mm, "end": v(45.27, -126.46) * mm, "construction": true});
            skLineSegment(sketch, "E74.MirrorCS", {"start": v(-39.35, -111.46) * mm, "end": v(-39.35, -126.46) * mm, "construction": true});
            skLineSegment(sketch, "E75.bottom", {"start": v(-39.35, -111.46) * mm, "end": v(45.27, -111.46) * mm});
            skLineSegment(sketch, "E75.top", {"start": v(-39.35, -126.46) * mm, "end": v(45.27, -126.46) * mm});
            skLineSegment(sketch, "E75.left", {"start": v(-39.35, -111.46) * mm, "end": v(-39.35, -126.46) * mm});
            skLineSegment(sketch, "E75.right", {"start": v(45.27, -111.46) * mm, "end": v(45.27, -126.46) * mm});
            skSolve(sketch);
        }
        {
            var Q0;
            Q0 = qSketchRegion(id + "F14", true);
            extrude(context, id + "F15", {"entities" : qUnion([Q0]), "operationType" : NewBodyOperationType.REMOVE, "endBound" : BoundingType.THROUGH_ALL, "depth" : 25 * mm, "offsetDistance" : 25 * mm, "hasDraft" : true, "draftAngle" : 6 * degree});
        }
        {
            var Q0;
            Q0=makeQuery(id+"F12.opExtrude","CAP_FACE",FACE,{"disambiguationData":[OSD([sQuery(id+"F2.wireOp",EDGE,"E13.left"),sQuery(id+"F11.wireOp",EDGE,"E53"),sQuery(id+"F11.wireOp",EDGE,"E54.MirrorCS"),sQuery(id+"F11.wireOp",EDGE,"E55")])],"isStart":false});
            var sketch = newSketch(context, id + "F16", { "sketchPlane" : qUnion([Q0])});
            skPoint(sketch, "E76", {"position": v(-111.46, 42.3) * mm});
            skPoint(sketch, "E77", {"position": v(-111.46, -42.3) * mm});
            skLineSegment(sketch, "E78", {"start": v(0, -25.6) * mm, "end": v(0, 32.78) * mm, "construction": true});
            skLineSegment(sketch, "E79", {"start": v(-111.46, 42.3) * mm, "end": v(-126.46, 42.3) * mm, "construction": true});
            skLineSegment(sketch, "E80", {"start": v(-111.46, -42.3) * mm, "end": v(-126.46, -42.3) * mm, "construction": true});
            skLineSegment(sketch, "E81.MirrorCS", {"start": v(111.46, 42.3) * mm, "end": v(126.46, 42.3) * mm, "construction": true});
            skLineSegment(sketch, "E82.MirrorCS", {"start": v(111.46, -42.3) * mm, "end": v(126.46, -42.3) * mm, "construction": true});
            skLineSegment(sketch, "E83.bottom", {"start": v(-126.46, 42.3) * mm, "end": v(-111.46, 42.3) * mm});
            skLineSegment(sketch, "E83.top", {"start": v(-126.46, -42.3) * mm, "end": v(-111.46, -42.3) * mm});
            skLineSegment(sketch, "E83.left", {"start": v(-126.46, 42.3) * mm, "end": v(-126.46, -42.3) * mm});
            skLineSegment(sketch, "E83.right", {"start": v(-111.46, 42.3) * mm, "end": v(-111.46, -42.3) * mm});
            skLineSegment(sketch, "E84.bottom", {"start": v(126.46, 42.3) * mm, "end": v(111.46, 42.3) * mm});
            skLineSegment(sketch, "E84.top", {"start": v(126.46, -42.3) * mm, "end": v(111.46, -42.3) * mm});
            skLineSegment(sketch, "E84.left", {"start": v(126.46, 42.3) * mm, "end": v(126.46, -42.3) * mm});
            skLineSegment(sketch, "E84.right", {"start": v(111.46, 42.3) * mm, "end": v(111.46, -42.3) * mm});
            skSolve(sketch);
        }
        {
            var Q0;
            Q0 = qSketchRegion(id + "F16", true);
            extrude(context, id + "F17", {"entities" : qUnion([Q0]), "operationType" : NewBodyOperationType.REMOVE, "endBound" : BoundingType.THROUGH_ALL, "depth" : 25 * mm, "offsetDistance" : 25 * mm, "hasDraft" : true, "draftAngle" : 6 * degree});
        }
    });
